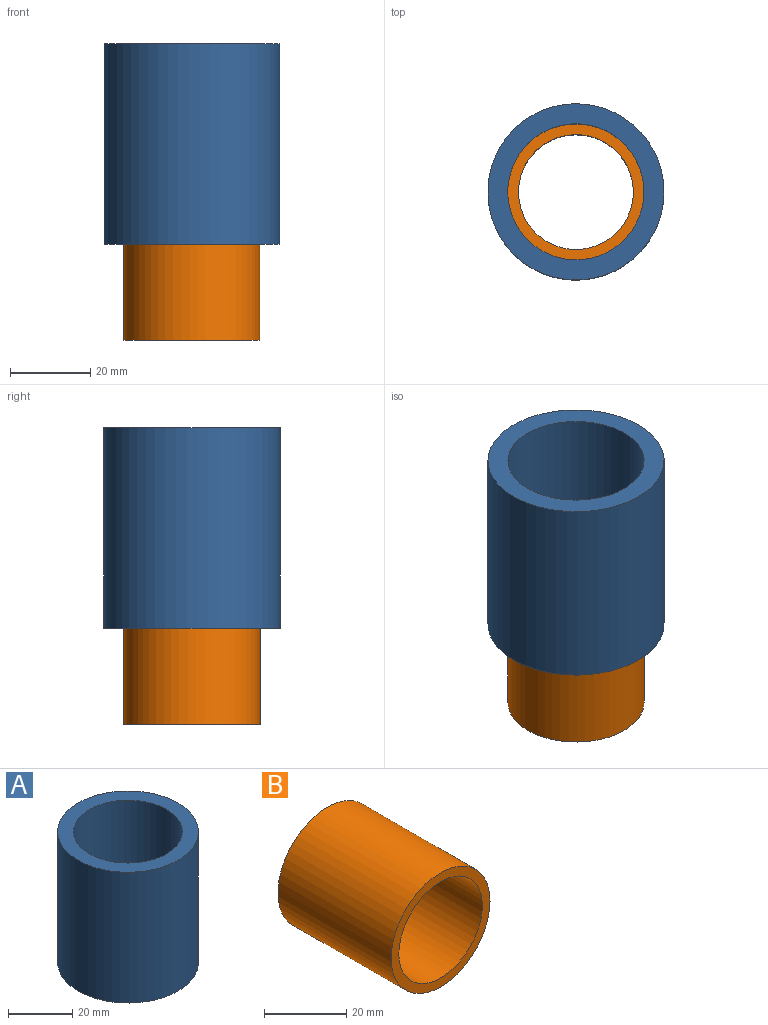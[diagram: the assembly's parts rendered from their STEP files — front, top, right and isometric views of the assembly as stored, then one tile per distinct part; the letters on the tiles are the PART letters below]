
ASSEMBLY  parts=2 mates=1
PART A: 4 faces, bbox 44x44x50 mm
  f0: cylinder r=17mm len=50mm, axis (0,0,-1), area 5340.7mm2, adj f2,f3
  f1: cylinder r=22mm len=50mm, axis (0,0,-1), area 6911.5mm2, adj f2,f3
  f2: plane 44x44mm, normal (0,0,1), area 612.6mm2, adj f0,f1
  f3: plane 44x44mm, normal (0,0,-1), area 612.6mm2, adj f0,f1
PART B: 4 faces, bbox 34x39x34 mm
  f0: cylinder r=14.35mm len=39mm, axis (0,1,0), area 3516.4mm2, adj f2,f3
  f1: cylinder r=17mm len=39mm, axis (0,1,0), area 4165.8mm2, adj f2,f3
  f2: plane 34x34mm, normal (0,-1,0), area 261mm2, adj f0,f1
  f3: plane 34x34mm, normal (0,1,0), area 261mm2, adj f0,f1
PLACE A t=(1.03,2.42,-12.26)mm
PLACE B rot(axis=(1,0,0),90deg) t=(1.03,2.42,2.74)mm
MATE fastened B.f0 <-> A.f0  axis (0,0,1) through (1.03,2.42,2.74)mm
